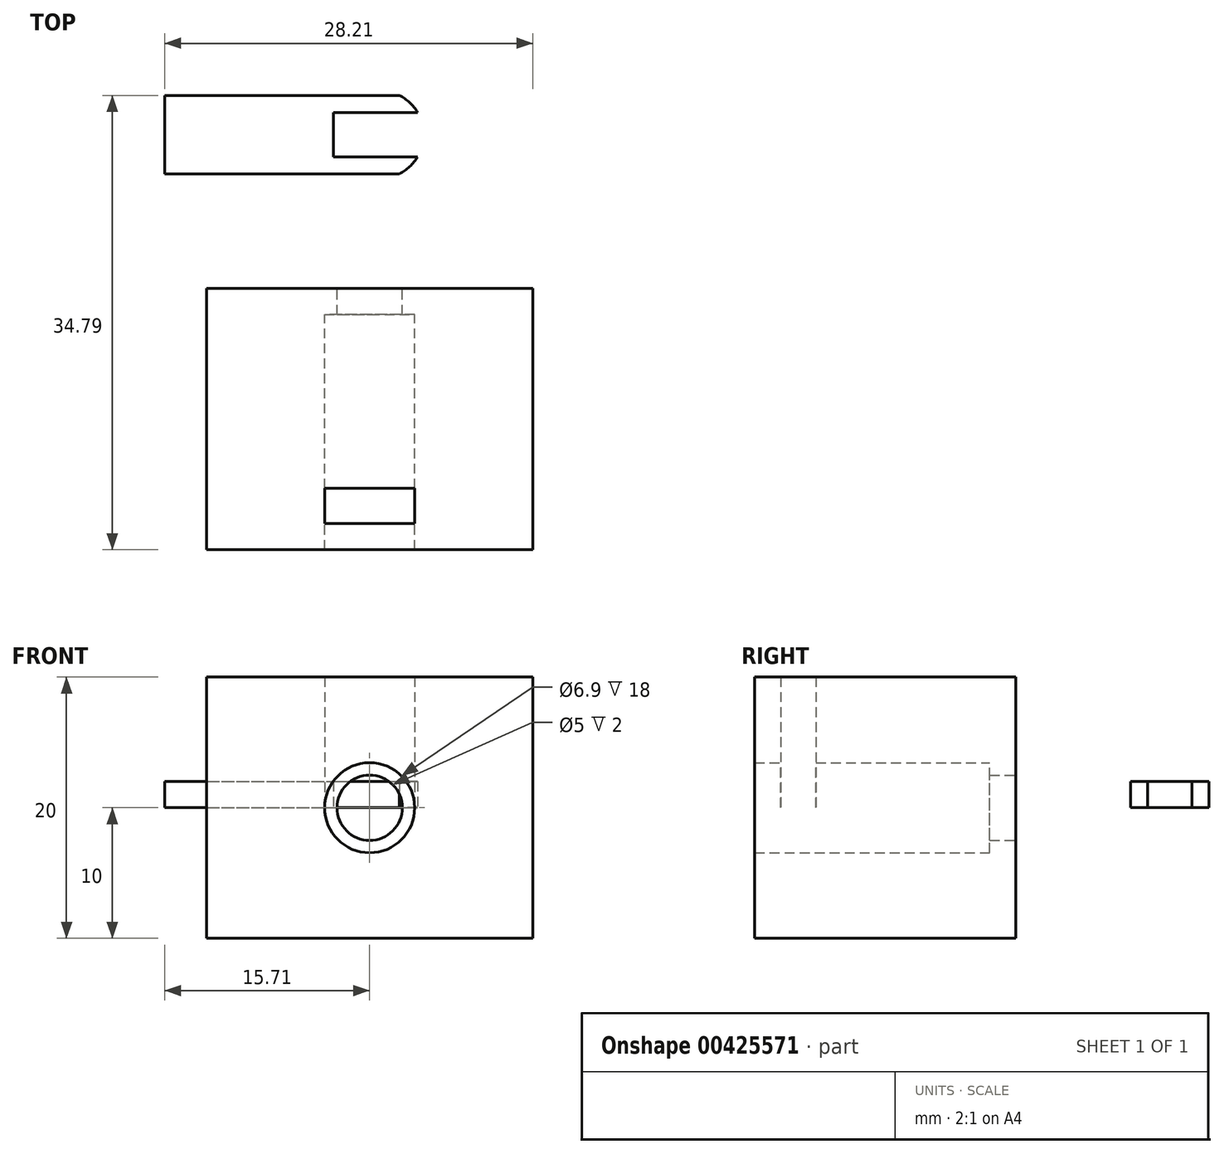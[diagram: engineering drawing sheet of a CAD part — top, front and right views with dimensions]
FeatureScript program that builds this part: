
annotation { "Feature Type Name" : "Feature", "Feature Type Description" : "" }
export const myFeature = defineFeature(function(context is Context, id is Id, definition is map)
    precondition{}
    {
        {
            var Q0;
            Q0=qCreatedBy(makeId("Front.planeOp"),FACE);
            var sketch = newSketch(context, id + "F0", { "sketchPlane" : qUnion([Q0])});
            skLineSegment(sketch, "E0.bottom", {"start": v(-12.5, -10) * mm, "end": v(12.5, -10) * mm});
            skLineSegment(sketch, "E0.top", {"start": v(-12.5, 10) * mm, "end": v(12.5, 10) * mm});
            skLineSegment(sketch, "E0.left", {"start": v(-12.5, -10) * mm, "end": v(-12.5, 10) * mm});
            skLineSegment(sketch, "E0.right", {"start": v(12.5, -10) * mm, "end": v(12.5, 10) * mm});
            skPoint(sketch, "E0.middle", {"position": v(0, 0) * mm});
            skSolve(sketch);
        }
        {
            var Q0;
            Q0=qCreatedBy(makeId("Front.planeOp"),FACE);
            var sketch = newSketch(context, id + "F1", { "sketchPlane" : qUnion([Q0])});
            skCircle(sketch, "E1", {"center": v(0, 0) * mm, "radius": 3.45 * mm});
            skSolve(sketch);
        }
        {
            var Q0;
            Q0=qCreatedBy(makeId("Front.planeOp"),FACE);
            var sketch = newSketch(context, id + "F2", { "sketchPlane" : qUnion([Q0])});
            skCircle(sketch, "E2", {"center": v(0, 0) * mm, "radius": 2.5 * mm});
            skSolve(sketch);
        }
        {
            var Q0;
            Q0 = qSketchRegion(id + "F0", true);
            extrude(context, id + "F3", {"entities" : qUnion([Q0]), "depth" : 20 * mm});
        }
        {
            var Q0;
            Q0 = qSketchRegion(id + "F1", true);
            extrude(context, id + "F4", {"entities" : qUnion([Q0]), "operationType" : NewBodyOperationType.REMOVE, "depth" : 37.2 * mm});
        }
        {
            var Q0;
            Q0 = qSketchRegion(id + "F1", true);
            extrude(context, id + "F5", {"entities" : qUnion([Q0]), "operationType" : NewBodyOperationType.ADD, "depth" : 2 * mm});
        }
        {
            var Q0;
            Q0 = qSketchRegion(id + "F2", true);
            extrude(context, id + "F6", {"entities" : qUnion([Q0]), "operationType" : NewBodyOperationType.REMOVE, "depth" : 2 * mm});
        }
        {
            var Q0;
            Q0=qCreatedBy(makeId("Top.planeOp"),FACE);
            var sketch = newSketch(context, id + "F7", { "sketchPlane" : qUnion([Q0])});
            skLineSegment(sketch, "E3.bottom", {"start": v(-3.45, -15.3) * mm, "end": v(3.45, -15.3) * mm});
            skLineSegment(sketch, "E3.top", {"start": v(-3.45, -18) * mm, "end": v(3.45, -18) * mm});
            skLineSegment(sketch, "E3.left", {"start": v(-3.45, -15.3) * mm, "end": v(-3.45, -18) * mm});
            skLineSegment(sketch, "E3.right", {"start": v(3.45, -15.3) * mm, "end": v(3.45, -18) * mm});
            skSolve(sketch);
        }
        {
            var Q0;
            Q0 = qSketchRegion(id + "F7", true);
            extrude(context, id + "F8", {"entities" : qUnion([Q0]), "operationType" : NewBodyOperationType.REMOVE, "depth" : 13.1 * mm});
        }
        {
            var Q0;
            Q0=qCreatedBy(makeId("Top.planeOp"),FACE);
            var sketch = newSketch(context, id + "F9", { "sketchPlane" : qUnion([Q0])});
            skLineSegment(sketch, "E4.bottom", {"start": v(-15.71, 14.79) * mm, "end": v(-0.71, 14.79) * mm});
            skLineSegment(sketch, "E4.top", {"start": v(-15.71, 8.79) * mm, "end": v(-0.71, 8.79) * mm});
            skLineSegment(sketch, "E4.left", {"start": v(-15.71, 14.79) * mm, "end": v(-15.71, 8.79) * mm});
            skLineSegment(sketch, "E4.right", {"start": v(-0.71, 14.79) * mm, "end": v(-0.71, 8.79) * mm});
            skCircle(sketch, "E5", {"center": v(0.78, 11.79) * mm, "radius": 3.35 * mm});
            skPoint(sketch, "E5.third.point", {"position": v(-2.57, 11.79) * mm});
            skPoint(sketch, "E5.third.point.positionSnap0", {"position": v(-0.71, 11.79) * mm});
            skSolve(sketch);
        }
        {
            var Q0;
            Q0 = qSketchRegion(id + "F9", true);
            extrude(context, id + "F10", {"entities" : qUnion([Q0]), "depth" : 2 * mm});
        }
        {
            var Q0;
            Q0=qCreatedBy(makeId("Top.planeOp"),FACE);
            var sketch = newSketch(context, id + "F11", { "sketchPlane" : qUnion([Q0])});
            skLineSegment(sketch, "E6.bottom", {"start": v(-2.78, 13.49) * mm, "end": v(4.22, 13.49) * mm});
            skLineSegment(sketch, "E6.top", {"start": v(-2.78, 10.09) * mm, "end": v(4.22, 10.09) * mm});
            skLineSegment(sketch, "E6.left", {"start": v(-2.78, 13.49) * mm, "end": v(-2.78, 10.09) * mm});
            skLineSegment(sketch, "E6.right", {"start": v(4.22, 13.49) * mm, "end": v(4.22, 10.09) * mm});
            skLineSegment(sketch, "E7.bottom", {"start": v(-1.96, 8.79) * mm, "end": v(2.61, 8.79) * mm});
            skLineSegment(sketch, "E7.top", {"start": v(-1.96, 7.04) * mm, "end": v(2.61, 7.04) * mm});
            skLineSegment(sketch, "E7.left", {"start": v(-1.96, 8.79) * mm, "end": v(-1.96, 7.04) * mm});
            skLineSegment(sketch, "E7.right", {"start": v(2.61, 8.79) * mm, "end": v(2.61, 7.04) * mm});
            skLineSegment(sketch, "E8.bottom", {"start": v(-1.9, 15.89) * mm, "end": v(2.9, 15.89) * mm});
            skLineSegment(sketch, "E8.top", {"start": v(-1.9, 14.79) * mm, "end": v(2.9, 14.79) * mm});
            skLineSegment(sketch, "E8.left", {"start": v(-1.9, 15.89) * mm, "end": v(-1.9, 14.79) * mm});
            skLineSegment(sketch, "E8.right", {"start": v(2.9, 15.89) * mm, "end": v(2.9, 14.79) * mm});
            skSolve(sketch);
        }
        {
            var Q0;
            Q0 = qSketchRegion(id + "F11", true);
            extrude(context, id + "F12", {"entities" : qUnion([Q0]), "operationType" : NewBodyOperationType.REMOVE, "depth" : 2 * mm});
        }
        {
            var Q0;
            Q0 = qSketchRegion(id + "F11", true);
            extrude(context, id + "F13", {"entities" : qUnion([Q0]), "operationType" : NewBodyOperationType.REMOVE, "depth" : 2 * mm});
        }
    });
